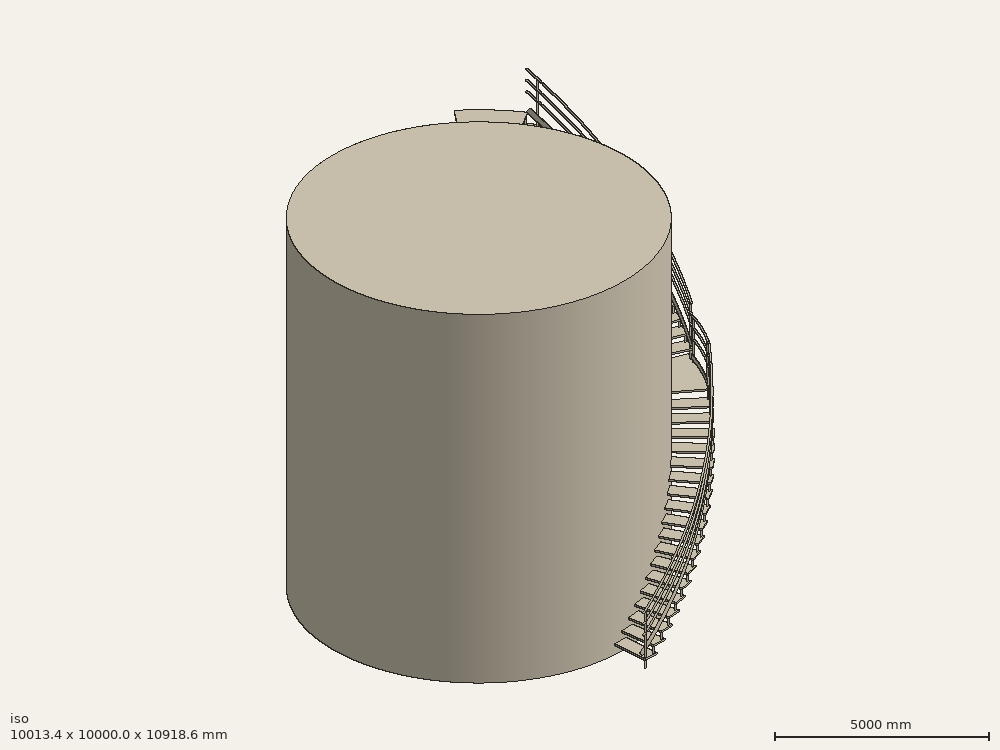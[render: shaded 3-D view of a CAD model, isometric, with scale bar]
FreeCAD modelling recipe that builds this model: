
FCSTD DOCUMENT  (FreeCAD 0.18R15419 (Git))
Label: BIG TANK HANDRAIL
License: CreativeCommons Attribution-NonCommercial-ShareAlike
LicenseURL: http://creativecommons.org/licenses/by-nc-sa/4.0/
objects: Part::FeaturePython×15, Part::Cylinder×6, Part::MultiFuse×4, Part::Sweep×3, Part::Compound×3, Part::Plane×2, Part::Box×1, Part::Helix×1, Part::Circle×1, Part::Torus×1
note: 37 computed .brp shape members not serialized (recipe doc carries the construction recipe); baked Part::Feature solids carry a one-line shape summary decoded from their .brp

FEATURE [Part::Box] Box  label="Cube"
  AttacherType = Attacher::AttachEngine3D
  Height = 50
  Length = 5500
  Placement = pos=(0,0,250) rot=(0,0,1;0rad)
  Width = 400
FEATURE [Part::Cylinder] Cylinder
  Angle = 360
  AttacherType = Attacher::AttachEngine3D
  Height = 250
  Placement = pos=(5450,50,0) rot=(0,0,1;0rad)
  Radius = 25
FEATURE [Part::MultiFuse] Fusion
  Shapes = -> [Box,Cylinder]
FEATURE [Part::FeaturePython] Clone  label="Fusion001"  # Draft clone (typed FeaturePython)
  AttacherType = Attacher::AttachEngine3D
  Fuse = false
  Objects = -> [Fusion]
  Placement = pos=(0,0,250) rot=(0,0,1;0.05236rad)
  Scale = (1,1,1)
FEATURE [Part::FeaturePython] Clone001  label="Fusion002"  # Draft clone (typed FeaturePython)
  AttacherType = Attacher::AttachEngine3D
  Fuse = false
  Objects = -> [Clone]
  Placement = pos=(0,0,500) rot=(0,0,1;0.10472rad)
  Scale = (1,1,1)
FEATURE [Part::FeaturePython] Clone002  label="Fusion003"  # Draft clone (typed FeaturePython)
  AttacherType = Attacher::AttachEngine3D
  Fuse = false
  Objects = -> [Clone001]
  Placement = pos=(0,0,750) rot=(0,0,1;0.15708rad)
  Scale = (1,1,1)
FEATURE [Part::FeaturePython] Clone003  label="Fusion004"  # Draft clone (typed FeaturePython)
  AttacherType = Attacher::AttachEngine3D
  Fuse = false
  Objects = -> [Clone002]
  Placement = pos=(0,0,1000) rot=(0,0,1;0.20944rad)
  Scale = (1,1,1)
FEATURE [Part::FeaturePython] Clone004  label="Fusion005"  # Draft clone (typed FeaturePython)
  AttacherType = Attacher::AttachEngine3D
  Fuse = false
  Objects = -> [Clone003]
  Placement = pos=(0,0,1250) rot=(0,0,1;0.261799rad)
  Scale = (1,1,1)
FEATURE [Part::MultiFuse] Fusion001  label="Fusion006"
  Shapes = -> [Fusion,Clone,Clone001,Clone002,Clone003,Clone004]
FEATURE [Part::FeaturePython] Clone005  label="Fusion007"  # Draft clone (typed FeaturePython)
  AttacherType = Attacher::AttachEngine3D
  Fuse = false
  Objects = -> [Fusion001]
  Placement = pos=(0,0,1500) rot=(0,0,1;0.314159rad)
  Scale = (1,1,1)
FEATURE [Part::FeaturePython] Clone006  label="Fusion008"  # Draft clone (typed FeaturePython)
  AttacherType = Attacher::AttachEngine3D
  Fuse = false
  Objects = -> [Clone005]
  Placement = pos=(0,0,3000) rot=(0,0,1;0.628319rad)
  Scale = (1,1,1)
FEATURE [Part::Cylinder] Cylinder001
  Angle = 18
  AttacherType = Attacher::AttachEngine3D
  Height = 50
  Placement = pos=(0,0,4800) rot=(0,0,1;0.942478rad)
  Radius = 5500
FEATURE [Part::Cylinder] Cylinder002
  Angle = 360
  AttacherType = Attacher::AttachEngine3D
  Height = 250
  Placement = pos=(3166.89,4435.73,4550) rot=(0,0,1;0.994838rad)
  Radius = 25
FEATURE [Part::MultiFuse] Fusion002  label="Fusion009"
  Shapes = -> [Fusion001,Clone005,Clone006,Cylinder001,Cylinder002]
FEATURE [Part::FeaturePython] Clone007  label="Fusion010"  # Draft clone (typed FeaturePython)
  AttacherType = Attacher::AttachEngine3D
  Fuse = false
  Objects = -> [Fusion002]
  Placement = pos=(0,0,4850) rot=(0,0,1;1.20428rad)
  Scale = (1,1,1)
FEATURE [Part::Cylinder] Cylinder003
  Angle = 360
  AttacherType = Attacher::AttachEngine3D
  Height = 9950
  Radius = 4500
FEATURE [Part::MultiFuse] Fusion003  label="Fusion011"
  Shapes = -> [Cylinder003,Clone007,Fusion002]
FEATURE [Part::Helix] Helix
  Angle = 0
  AttacherType = Attacher::AttachEngine3D
  Height = 4550
  LocalCoord = 0
  Pitch = 30200
  Radius = 5450
  Style = 1
FEATURE [Part::Circle] Circle
  Angle0 = 0
  Angle1 = 360
  AttacherType = Attacher::AttachEngine3D
  Placement = pos=(5450,0,0) rot=(-1,0,0;0.837758rad)
  Radius = 25
FEATURE [Part::Plane] Plane
  AttacherType = Attacher::AttachEngine3D
  Length = 5
  Placement = pos=(5420,0,0) rot=(1,0,0;2.30383rad)
  Width = 150
FEATURE [Part::Sweep] Sweep
  Frenet = true
  Placement = pos=(0,0,900) rot=(0,0,1;0rad)
  Sections = -> [Circle]
  Solid = true
  Spine = -> Helix [Edge1]
  Transition = 0
FEATURE [Part::Sweep] Sweep001
  Frenet = true
  Placement = pos=(0,0,350) rot=(0,0,1;0rad)
  Sections = -> [Plane]
  Solid = true
  Spine = -> Helix [Edge1]
  Transition = 0
FEATURE [Part::FeaturePython] Clone008  label="Sweep002"  # Draft clone (typed FeaturePython)
  AttacherType = Attacher::AttachEngine3D
  Fuse = false
  Objects = -> [Sweep]
  Placement = pos=(0,0,1200) rot=(0,0,1;0rad)
  Scale = (1,1,1)
FEATURE [Part::FeaturePython] Clone009  label="Sweep003"  # Draft clone (typed FeaturePython)
  AttacherType = Attacher::AttachEngine3D
  Fuse = false
  Objects = -> [Clone008]
  Placement = pos=(0,0,1500) rot=(0,0,1;0rad)
  Scale = (1,1,1)
FEATURE [Part::Cylinder] Cylinder004
  Angle = 360
  AttacherType = Attacher::AttachEngine3D
  Height = 1250
  Placement = pos=(5446,70.8081,300) rot=(0,0,1;0.069813rad)
  Radius = 25
FEATURE [Part::FeaturePython] Clone010  label="Cylinder005"  # Draft clone (typed FeaturePython)
  AttacherType = Attacher::AttachEngine3D
  Fuse = false
  Objects = -> [Cylinder004]
  Placement = pos=(3396.69,4257.77,4550) rot=(0,0,1;0.837758rad)
  Scale = (1,1,1)
FEATURE [Part::Compound] Compound
  Links = -> [Clone010,Cylinder004,Clone009,Clone008,Sweep001,Sweep]
FEATURE [Part::FeaturePython] Clone011  label="Compound001"  # Draft clone (typed FeaturePython)
  AttacherType = Attacher::AttachEngine3D
  Fuse = false
  Objects = -> [Compound]
  Placement = pos=(0,0,4850) rot=(0,0,1;1.20428rad)
  Scale = (1,1,1)
FEATURE [Part::Plane] Plane001
  AttacherType = Attacher::AttachEngine3D
  Length = 5
  Placement = pos=(5420,0,0) rot=(1,0,0;1.5708rad)
  Width = 150
FEATURE [Part::Torus] Torus
  Angle1 = -180
  Angle2 = 180
  Angle3 = 13.5
  AttacherType = Attacher::AttachEngine3D
  Placement = pos=(0,0,600) rot=(0,0,1;0rad)
  Radius1 = 5450
  Radius2 = 25
FEATURE [Part::Sweep] Sweep002  label="Sweep004"
  Frenet = true
  Placement = pos=(0,0,50) rot=(0,0,1;0rad)
  Sections = -> [Plane001]
  Solid = true
  Spine = -> Torus [Edge1]
  Transition = 1
FEATURE [Part::Cylinder] Cylinder005  label="Cylinder006"
  Angle = 360
  AttacherType = Attacher::AttachEngine3D
  Height = 1200
  Placement = pos=(5449,50,0) rot=(0,0,1;0rad)
  Radius = 25
FEATURE [Part::FeaturePython] Clone012  label="Cylinder007"  # Draft clone (typed FeaturePython)
  AttacherType = Attacher::AttachEngine3D
  Fuse = false
  Objects = -> [Cylinder005]
  Placement = pos=(5313.21,1211.02,0) rot=(0,0,1;0.20944rad)
  Scale = (1,1,1)
FEATURE [Part::FeaturePython] Clone013  label="Torus001"  # Draft clone (typed FeaturePython)
  AttacherType = Attacher::AttachEngine3D
  Fuse = false
  Objects = -> [Torus]
  Placement = pos=(0,0,900) rot=(0,0,1;0rad)
  Scale = (1,1,1)
FEATURE [Part::FeaturePython] Clone014  label="Torus002"  # Draft clone (typed FeaturePython)
  AttacherType = Attacher::AttachEngine3D
  Fuse = false
  Objects = -> [Clone013]
  Placement = pos=(0,0,1200) rot=(0,0,1;0rad)
  Scale = (1,1,1)
FEATURE [Part::Compound] Compound001  label="Compound002"
  Links = -> [Clone014,Clone013,Clone012,Cylinder005,Sweep002,Torus]
  Placement = pos=(0,0,4850) rot=(0,0,1;0.959931rad)
FEATURE [Part::Compound] Compound002  label="Compound003"
  Links = -> [Compound001,Clone011,Compound,Fusion003]
  Placement = pos=(0,0,0) rot=(0,0,1;4.71239rad)
